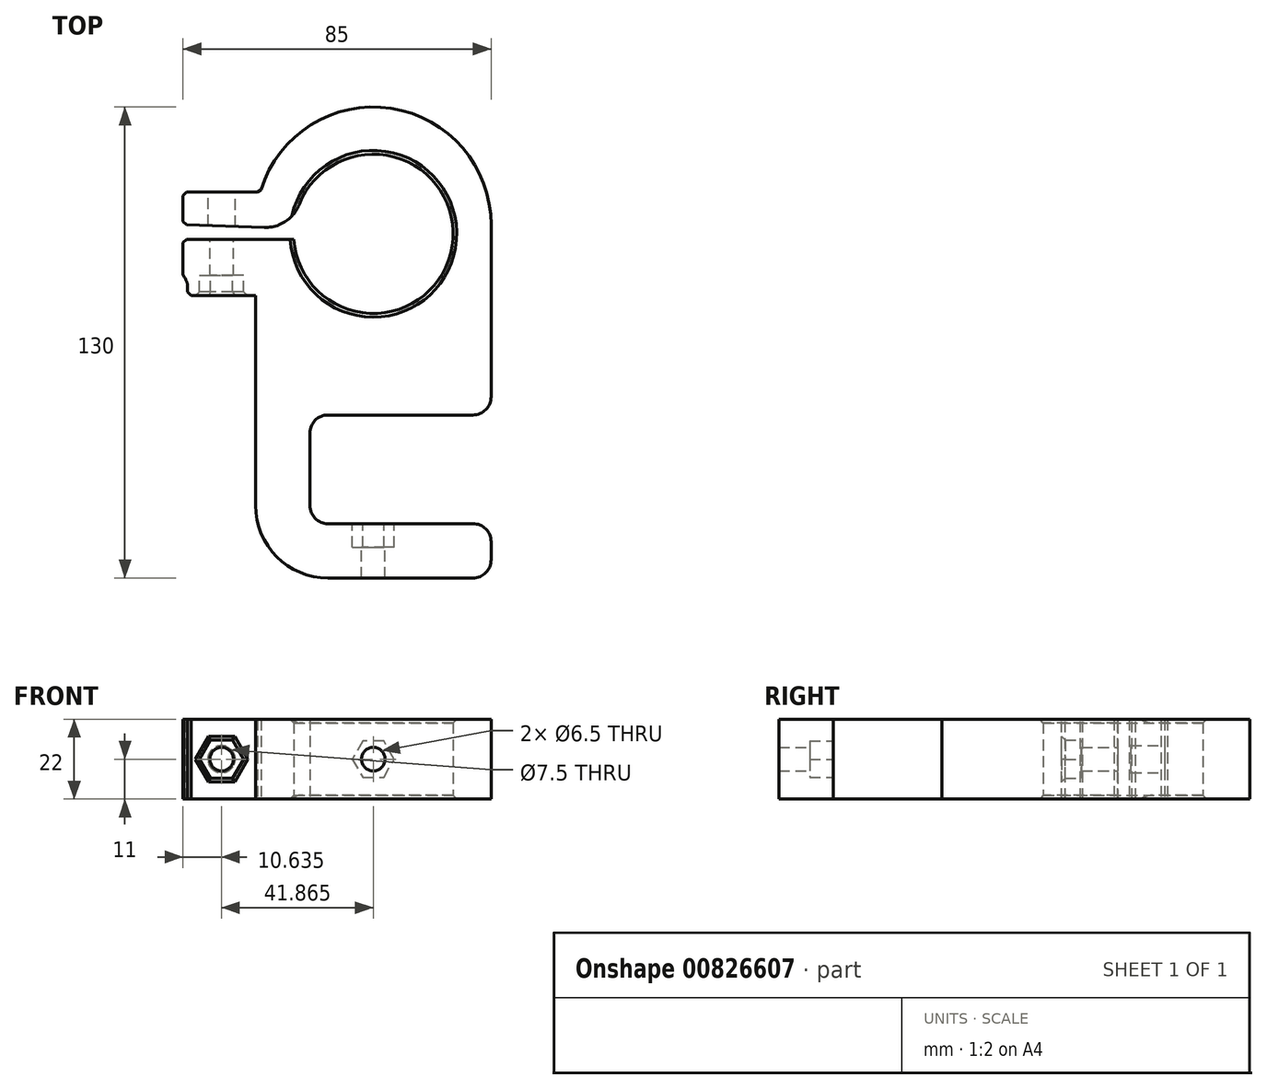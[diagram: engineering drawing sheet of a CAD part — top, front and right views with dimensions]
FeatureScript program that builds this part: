
annotation { "Feature Type Name" : "Feature", "Feature Type Description" : "" }
export const myFeature = defineFeature(function(context is Context, id is Id, definition is map)
    precondition{}
    {
        {
            var Q0;
            Q0=qCreatedBy(makeId("Top.planeOp"),FACE);
            var sketch = newSketch(context, id + "F0", { "sketchPlane" : qUnion([Q0])});
            skLineSegment(sketch, "E0", {"start": v(0, 0) * mm, "end": v(-50, 0) * mm});
            skLineSegment(sketch, "E1", {"start": v(-50, 0) * mm, "end": v(-50, 30) * mm});
            skLineSegment(sketch, "E2", {"start": v(-50, 30) * mm, "end": v(0, 30) * mm});
            skLineSegment(sketch, "E3", {"start": v(0, 0) * mm, "end": v(0, -15) * mm});
            skLineSegment(sketch, "E4", {"start": v(0, -15) * mm, "end": v(-65, -15) * mm});
            skLineSegment(sketch, "E5", {"start": v(-65, -15) * mm, "end": v(-65, 78.5) * mm});
            skLineSegment(sketch, "E6", {"start": v(-65, 78.5) * mm, "end": v(-54.45, 78.5) * mm});
            skArc(sketch, "E7", {"start": v(-54.45, 78.5) * mm, "mid": v(-10.5, 80) * mm, "end": v(-54.45, 81.5) * mm});
            skLineSegment(sketch, "E8", {"start": v(-54.45, 81.5) * mm, "end": v(-65, 81.5) * mm});
            skLineSegment(sketch, "E9", {"start": v(-65, 81.5) * mm, "end": v(-65, 115) * mm});
            skLineSegment(sketch, "E10", {"start": v(-65, 115) * mm, "end": v(0, 115) * mm});
            skLineSegment(sketch, "E11", {"start": v(0, 115) * mm, "end": v(0, 30) * mm});
            skSolve(sketch);
        }
        {
            var Q0;
            Q0 = qSketchRegion(id + "F0", true);
            extrude(context, id + "F1", {"entities" : qUnion([Q0]), "depth" : 22 * mm, "offsetDistance" : 25 * mm});
        }
        {
            var Q0;
            Q0=makeQuery(id+"F1.opExtrude","SWEPT_EDGE",EDGE,{"disambiguationData":[OSD([sQuery(id+"F0.wireOp",EDGE,"E9"),sQuery(id+"F0.wireOp",EDGE,"E10")])]});
            var Q1;
            Q1=makeQuery(id+"F1.opExtrude","SWEPT_EDGE",EDGE,{"disambiguationData":[OSD([sQuery(id+"F0.wireOp",EDGE,"E10"),sQuery(id+"F0.wireOp",EDGE,"E11")])]});
            fillet(context, id + "F2", {"entities" : qUnion([Q0, Q1]), "radius" : 32.5 * mm, "tangentPropagation" : true, "allowEdgeOverflow" : false});
        }
        {
            var Q0;
            Q0=makeQuery(id+"F1.opExtrude","CAP_EDGE",EDGE,{"disambiguationData":[OSD([sQuery(id+"F0.wireOp",EDGE,"E7")])],"isStart":false});
            var Q1;
            Q1=makeQuery(id+"F1.opExtrude","CAP_EDGE",EDGE,{"disambiguationData":[OSD([sQuery(id+"F0.wireOp",EDGE,"E7")])],"isStart":true});
            chamfer(context, id + "F3", {"entities" : qUnion([Q0, Q1]), "width" : 1 * mm, "tangentPropagation" : true});
        }
        {
            var Q0;
            Q0=makeQuery(id+"F1.opExtrude","SWEPT_FACE",FACE,{"disambiguationData":[OSD([sQuery(id+"F0.wireOp",EDGE,"E5")])]});
            var sketch = newSketch(context, id + "F4", { "sketchPlane" : qUnion([Q0])});
            skLineSegment(sketch, "E12.bottom", {"start": v(-78.5, 0) * mm, "end": v(-68.5, 0) * mm});
            skLineSegment(sketch, "E12.top", {"start": v(-78.5, 22) * mm, "end": v(-68.5, 22) * mm});
            skLineSegment(sketch, "E12.left", {"start": v(-78.5, 0) * mm, "end": v(-78.5, 22) * mm});
            skLineSegment(sketch, "E12.right", {"start": v(-68.5, 0) * mm, "end": v(-68.5, 22) * mm});
            skSolve(sketch);
        }
        {
            var Q0;
            Q0 = qSketchRegion(id + "F4", true);
            extrude(context, id + "F5", {"entities" : qUnion([Q0]), "operationType" : NewBodyOperationType.ADD, "depth" : 20 * mm, "offsetDistance" : 25 * mm});
        }
        {
            var Q0;
            Q0=makeQuery(id+"F1.opExtrude","SWEPT_FACE",FACE,{"disambiguationData":[OSD([sQuery(id+"F0.wireOp",EDGE,"E9")])]});
            var sketch = newSketch(context, id + "F6", { "sketchPlane" : qUnion([Q0])});
            skLineSegment(sketch, "E13.bottom", {"start": v(-81.5, 0) * mm, "end": v(-91.5, 0) * mm});
            skLineSegment(sketch, "E13.top", {"start": v(-81.5, 22) * mm, "end": v(-91.5, 22) * mm});
            skLineSegment(sketch, "E13.left", {"start": v(-81.5, 0) * mm, "end": v(-81.5, 22) * mm});
            skLineSegment(sketch, "E13.right", {"start": v(-91.5, 0) * mm, "end": v(-91.5, 22) * mm});
            skSolve(sketch);
        }
        {
            var Q0;
            Q0 = qSketchRegion(id + "F6", true);
            extrude(context, id + "F7", {"entities" : qUnion([Q0]), "operationType" : NewBodyOperationType.ADD, "depth" : 20 * mm, "offsetDistance" : 25 * mm, "hasSecondDirection" : true, "secondDirectionOppositeDirection" : true, "secondDirectionDepth" : 2 * mm});
        }
        {
            var Q0;
            Q0=makeQuery(id+"F7.opExtrude","CAP_EDGE",EDGE,{"disambiguationData":[OSD([sQuery(id+"F6.wireOp",EDGE,"E13.left")])],"isStart":false});
            chamfer(context, id + "F8", {"entities" : qUnion([Q0]), "chamferType" : ChamferType.TWO_OFFSETS, "width1" : 30 * mm, "oppositeDirection" : false, "width2" : 1 * mm, "tangentPropagation" : true});
        }
        {
            var Q0;
            Q0=makeQuery(id+"F7.opExtrude","SWEPT_FACE",FACE,{"disambiguationData":[OSD([sQuery(id+"F6.wireOp",EDGE,"E13.right")])]});
            var sketch = newSketch(context, id + "F9", { "sketchPlane" : qUnion([Q0])});
            skLineSegment(sketch, "E14", {"start": v(85, 0) * mm, "end": v(63.73, 22) * mm, "construction": true});
            skCircle(sketch, "E15", {"center": v(74.36, 11) * mm, "radius": 3.25 * mm});
            skSolve(sketch);
        }
        {
            var Q0;
            Q0 = qSketchRegion(id + "F9", true);
            extrude(context, id + "F10", {"entities" : qUnion([Q0]), "operationType" : NewBodyOperationType.REMOVE, "endBound" : BoundingType.THROUGH_ALL, "oppositeDirection" : true, "depth" : 25 * mm, "offsetDistance" : 25 * mm});
        }
        {
            var Q0;
            Q0=makeQuery(id+"F5.opExtrude","SWEPT_FACE",FACE,{"disambiguationData":[OSD([sQuery(id+"F4.wireOp",EDGE,"E12.right")])]});
            var sketch = newSketch(context, id + "F11", { "sketchPlane" : qUnion([Q0])});
            skCircle(sketch, "E16.cCircle", {"center": v(-74.36, 11) * mm, "radius": 5.25 * mm, "construction": true});
            skLineSegment(sketch, "E16.0", {"start": v(-77.4, 16.25) * mm, "end": v(-71.33, 16.25) * mm});
            skLineSegment(sketch, "E16.1", {"start": v(-71.33, 16.25) * mm, "end": v(-68.3, 11) * mm});
            skLineSegment(sketch, "E16.2", {"start": v(-68.3, 11) * mm, "end": v(-71.33, 5.75) * mm});
            skLineSegment(sketch, "E16.3", {"start": v(-71.33, 5.75) * mm, "end": v(-77.4, 5.75) * mm});
            skLineSegment(sketch, "E16.4", {"start": v(-77.4, 5.75) * mm, "end": v(-80.43, 11) * mm});
            skLineSegment(sketch, "E16.5", {"start": v(-80.43, 11) * mm, "end": v(-77.4, 16.25) * mm});
            skPoint(sketch, "E16.0.midPoint", {"position": v(-74.36, 16.25) * mm});
            skLineSegment(sketch, "E17.bottom", {"start": v(-83.73, 22) * mm, "end": v(-65, 22) * mm});
            skLineSegment(sketch, "E17.top", {"start": v(-83.73, 0) * mm, "end": v(-65, 0) * mm});
            skLineSegment(sketch, "E17.left", {"start": v(-83.73, 22) * mm, "end": v(-83.73, 0) * mm});
            skLineSegment(sketch, "E17.right", {"start": v(-65, 22) * mm, "end": v(-65, 0) * mm});
            skSolve(sketch);
        }
        {
            var Q0;
            Q0 = qSketchRegion(id + "F11", true);
            extrude(context, id + "F12", {"entities" : qUnion([Q0]), "operationType" : NewBodyOperationType.ADD, "depth" : 5.5 * mm, "offsetDistance" : 25 * mm});
        }
        {
            var Q0;
            Q0=makeQuery(id+"F1.opExtrude","SWEPT_EDGE",EDGE,{"disambiguationData":[OSD([sQuery(id+"F0.wireOp",EDGE,"E4"),sQuery(id+"F0.wireOp",EDGE,"E5")])]});
            fillet(context, id + "F13", {"entities" : qUnion([Q0]), "radius" : 20 * mm, "tangentPropagation" : true, "allowEdgeOverflow" : false});
        }
        {
            var Q0;
            Q0=makeQuery(id+"F1.opExtrude","SWEPT_EDGE",EDGE,{"disambiguationData":[OSD([sQuery(id+"F0.wireOp",EDGE,"E0"),sQuery(id+"F0.wireOp",EDGE,"E1")])]});
            var Q1;
            Q1=makeQuery(id+"F1.opExtrude","SWEPT_EDGE",EDGE,{"disambiguationData":[OSD([sQuery(id+"F0.wireOp",EDGE,"E1"),sQuery(id+"F0.wireOp",EDGE,"E2")])]});
            fillet(context, id + "F14", {"entities" : qUnion([Q0, Q1]), "radius" : 5 * mm, "tangentPropagation" : true, "allowEdgeOverflow" : false});
        }
        {
            var Q0;
            Q0=makeQuery(id+"F1.opExtrude","SWEPT_FACE",FACE,{"disambiguationData":[OSD([sQuery(id+"F0.wireOp",EDGE,"E0")])]});
            var sketch = newSketch(context, id + "F15", { "sketchPlane" : qUnion([Q0])});
            skLineSegment(sketch, "E18", {"start": v(0, 11) * mm, "end": v(45, 11) * mm, "construction": true});
            skLineSegment(sketch, "E19.0.0", {"start": v(54.45, 21) * mm, "end": v(54.45, 1) * mm});
            skLineSegment(sketch, "E19.0.1", {"start": v(54.45, 1) * mm, "end": v(10.5, 1) * mm, "construction": true});
            skLineSegment(sketch, "E19.0.2", {"start": v(54.45, 1) * mm, "end": v(54.45, 21) * mm, "construction": true});
            skLineSegment(sketch, "E19.0.3", {"start": v(54.45, 21) * mm, "end": v(10.5, 21) * mm, "construction": true});
            skCircle(sketch, "E20", {"center": v(32.5, 11) * mm, "radius": 3.25 * mm});
            skSolve(sketch);
        }
        {
            var Q0;
            Q0 = qSketchRegion(id + "F15", true);
            var Q1;
            Q1=makeQuery(id+"F1.opExtrude","SWEPT_FACE",FACE,{"disambiguationData":[OSD([sQuery(id+"F0.wireOp",EDGE,"E4")])]});
            extrude(context, id + "F16", {"entities" : qUnion([Q0]), "operationType" : NewBodyOperationType.REMOVE, "endBound" : BoundingType.UP_TO_SURFACE, "oppositeDirection" : true, "depth" : 25 * mm, "endBoundEntityFace" : qUnion([Q1]), "offsetDistance" : 25 * mm});
        }
        {
            var Q0;
            Q0=makeQuery(id+"F1.opExtrude","SWEPT_FACE",FACE,{"disambiguationData":[OSD([sQuery(id+"F0.wireOp",EDGE,"E0")])]});
            var sketch = newSketch(context, id + "F17", { "sketchPlane" : qUnion([Q0])});
            skCircle(sketch, "E21.cCircle", {"center": v(32.5, 11) * mm, "radius": 5 * mm, "construction": true});
            skLineSegment(sketch, "E21.0", {"start": v(35.39, 6) * mm, "end": v(29.61, 6) * mm});
            skLineSegment(sketch, "E21.1", {"start": v(29.61, 6) * mm, "end": v(26.73, 11) * mm});
            skLineSegment(sketch, "E21.2", {"start": v(26.73, 11) * mm, "end": v(29.61, 16) * mm});
            skLineSegment(sketch, "E21.3", {"start": v(29.61, 16) * mm, "end": v(35.39, 16) * mm});
            skLineSegment(sketch, "E21.4", {"start": v(35.39, 16) * mm, "end": v(38.27, 11) * mm});
            skLineSegment(sketch, "E21.5", {"start": v(38.27, 11) * mm, "end": v(35.39, 6) * mm});
            skPoint(sketch, "E21.0.midPoint", {"position": v(32.5, 6) * mm});
            skSolve(sketch);
        }
        {
            var Q0;
            Q0 = qSketchRegion(id + "F17", true);
            extrude(context, id + "F18", {"entities" : qUnion([Q0]), "operationType" : NewBodyOperationType.REMOVE, "oppositeDirection" : true, "depth" : 6.5 * mm, "offsetDistance" : 25 * mm});
        }
        {
            var Q0;
            Q0=makeQuery(id+"F18.boolean.opBoolean","COPY",EDGE,{"derivedFrom":makeQuery(id+"F18.opExtrude","CAP_EDGE",EDGE,{"disambiguationData":[OSD([sQuery(id+"F17.wireOp",EDGE,"E21.0")])],"isStart":true})});
            var Q1;
            Q1=makeQuery(id+"F18.boolean.opBoolean","COPY",EDGE,{"derivedFrom":makeQuery(id+"F18.opExtrude","CAP_EDGE",EDGE,{"disambiguationData":[OSD([sQuery(id+"F17.wireOp",EDGE,"E21.1")])],"isStart":true})});
            var Q2;
            Q2=makeQuery(id+"F18.boolean.opBoolean","COPY",EDGE,{"derivedFrom":makeQuery(id+"F18.opExtrude","CAP_EDGE",EDGE,{"disambiguationData":[OSD([sQuery(id+"F17.wireOp",EDGE,"E21.2")])],"isStart":true})});
            var Q3;
            Q3=makeQuery(id+"F18.boolean.opBoolean","COPY",EDGE,{"derivedFrom":makeQuery(id+"F18.opExtrude","CAP_EDGE",EDGE,{"disambiguationData":[OSD([sQuery(id+"F17.wireOp",EDGE,"E21.3")])],"isStart":true})});
            var Q4;
            Q4=makeQuery(id+"F18.boolean.opBoolean","COPY",EDGE,{"derivedFrom":makeQuery(id+"F18.opExtrude","CAP_EDGE",EDGE,{"disambiguationData":[OSD([sQuery(id+"F17.wireOp",EDGE,"E21.4")])],"isStart":true})});
            var Q5;
            Q5=makeQuery(id+"F18.boolean.opBoolean","COPY",EDGE,{"derivedFrom":makeQuery(id+"F18.opExtrude","CAP_EDGE",EDGE,{"disambiguationData":[OSD([sQuery(id+"F17.wireOp",EDGE,"E21.5")])],"isStart":true})});
            var Q6;
            Q6=makeQuery(id+"F12.opExtrude","CAP_EDGE",EDGE,{"disambiguationData":[OSD([sQuery(id+"F11.wireOp",EDGE,"E16.3")])],"isStart":false});
            var Q7;
            Q7=makeQuery(id+"F12.opExtrude","CAP_EDGE",EDGE,{"disambiguationData":[OSD([sQuery(id+"F11.wireOp",EDGE,"E16.2")])],"isStart":false});
            var Q8;
            Q8=makeQuery(id+"F12.opExtrude","CAP_EDGE",EDGE,{"disambiguationData":[OSD([sQuery(id+"F11.wireOp",EDGE,"E16.1")])],"isStart":false});
            var Q9;
            Q9=makeQuery(id+"F12.opExtrude","CAP_EDGE",EDGE,{"disambiguationData":[OSD([sQuery(id+"F11.wireOp",EDGE,"E16.0")])],"isStart":false});
            var Q10;
            Q10=makeQuery(id+"F12.opExtrude","CAP_EDGE",EDGE,{"disambiguationData":[OSD([sQuery(id+"F11.wireOp",EDGE,"E16.5")])],"isStart":false});
            var Q11;
            Q11=makeQuery(id+"F12.opExtrude","CAP_EDGE",EDGE,{"disambiguationData":[OSD([sQuery(id+"F11.wireOp",EDGE,"E16.4")])],"isStart":false});
            chamfer(context, id + "F19", {"entities" : qUnion([Q0, Q1, Q2, Q3, Q4, Q5, Q6, Q7, Q8, Q9, Q10, Q11]), "width" : 1 * mm, "tangentPropagation" : true});
        }
        {
            var Q0;
            Q0=makeQuery(id+"F12.opExtrude","CAP_EDGE",EDGE,{"disambiguationData":[OSD([sQuery(id+"F11.wireOp",EDGE,"E17.left")])],"isStart":true});
            fillet(context, id + "F20", {"entities" : qUnion([Q0]), "radius" : 5 * mm, "tangentPropagation" : true, "allowEdgeOverflow" : false});
        }
        {
            var Q0;
            Q0=makeQuery(id+"F7.opExtrude","CAP_EDGE",EDGE,{"disambiguationData":[OSD([sQuery(id+"F6.wireOp",EDGE,"E13.right")])],"isStart":false});
            var Q1;
            {var subQ0=sQuery(id+"F6.wireOp",EDGE,"E13.left");Q1=makeQuery(id+"F8.opChamfer","BLEND_EDGE",EDGE,{"blendedFrom":[makeQuery(id+"F7.opExtrude","CAP_EDGE",EDGE,{"disambiguationData":[OSD([subQ0])],"isStart":false}),makeQuery(id+"F7.opExtrude","CAP_FACE",FACE,{"disambiguationData":[OSD([sQuery(id+"F6.wireOp",EDGE,"E13.bottom"),sQuery(id+"F6.wireOp",EDGE,"E13.top"),subQ0,sQuery(id+"F6.wireOp",EDGE,"E13.right")])],"isStart":false})],"blendedInto":[makeQuery(id+"F7.opExtrude","CAP_FACE",FACE,{"disambiguationData":[OSD([sQuery(id+"F6.wireOp",EDGE,"E13.bottom"),sQuery(id+"F6.wireOp",EDGE,"E13.top"),subQ0,sQuery(id+"F6.wireOp",EDGE,"E13.right")])],"isStart":false})]});}
            var Q2;
            Q2=makeQuery(id+"F5.opExtrude","CAP_EDGE",EDGE,{"disambiguationData":[OSD([sQuery(id+"F4.wireOp",EDGE,"E12.left")])],"isStart":false});
            var Q3;
            Q3=makeQuery(id+"F20.opFillet","BLEND_EDGE",EDGE,{"blendedFrom":[makeQuery(id+"F12.opExtrude","CAP_EDGE",EDGE,{"disambiguationData":[OSD([sQuery(id+"F11.wireOp",EDGE,"E17.left")])],"isStart":true}),makeQuery(id+"F5.opExtrude","CAP_FACE",FACE,{"disambiguationData":[OSD([sQuery(id+"F4.wireOp",EDGE,"E12.bottom"),sQuery(id+"F4.wireOp",EDGE,"E12.top"),sQuery(id+"F4.wireOp",EDGE,"E12.left"),sQuery(id+"F4.wireOp",EDGE,"E12.right")])],"isStart":false})],"blendedInto":[makeQuery(id+"F5.opExtrude","CAP_FACE",FACE,{"disambiguationData":[OSD([sQuery(id+"F4.wireOp",EDGE,"E12.bottom"),sQuery(id+"F4.wireOp",EDGE,"E12.top"),sQuery(id+"F4.wireOp",EDGE,"E12.left"),sQuery(id+"F4.wireOp",EDGE,"E12.right")])],"isStart":false})]});
            var Q4;
            Q4=makeQuery(id+"F12.opExtrude","CAP_EDGE",EDGE,{"disambiguationData":[OSD([sQuery(id+"F11.wireOp",EDGE,"E17.left")])],"isStart":false});
            chamfer(context, id + "F21", {"entities" : qUnion([Q0, Q1, Q2, Q3, Q4]), "width" : 1 * mm, "tangentPropagation" : true});
        }
        {
            var Q0;
            Q0=makeQuery(id+"F7.boolean.opBoolean","INTERSECT",EDGE,{"derivedFrom":[makeQuery(id+"F2.opFillet","BLEND_FACE",FACE,{"disambiguationData":[OSD([sQuery(id+"F0.wireOp",EDGE,"E10"),sQuery(id+"F0.wireOp",EDGE,"E11")])]}),makeQuery(id+"F7.opExtrude","SWEPT_FACE",FACE,{"disambiguationData":[OSD([sQuery(id+"F6.wireOp",EDGE,"E13.right")])]})]});
            var Q1;
            Q1=makeQuery(id+"F12.opExtrude","CAP_EDGE",EDGE,{"disambiguationData":[OSD([sQuery(id+"F11.wireOp",EDGE,"E17.right")])],"isStart":false});
            chamfer(context, id + "F22", {"entities" : qUnion([Q0, Q1]), "width" : 1 * mm, "tangentPropagation" : true});
        }
        {
            var Q0;
            Q0=makeQuery(id+"F1.opExtrude","SWEPT_EDGE",EDGE,{"disambiguationData":[OSD([sQuery(id+"F0.wireOp",EDGE,"E2"),sQuery(id+"F0.wireOp",EDGE,"E11")])]});
            var Q1;
            Q1=makeQuery(id+"F1.opExtrude","SWEPT_EDGE",EDGE,{"disambiguationData":[OSD([sQuery(id+"F0.wireOp",EDGE,"E0"),sQuery(id+"F0.wireOp",EDGE,"E3")])]});
            fillet(context, id + "F23", {"entities" : qUnion([Q0, Q1]), "radius" : 5 * mm, "tangentPropagation" : true, "allowEdgeOverflow" : false});
        }
        {
            var Q0;
            Q0=makeQuery(id+"F1.opExtrude","SWEPT_EDGE",EDGE,{"disambiguationData":[OSD([sQuery(id+"F0.wireOp",EDGE,"E7"),sQuery(id+"F0.wireOp",EDGE,"E8")])]});
            fillet(context, id + "F24", {"entities" : qUnion([Q0]), "radius" : 10 * mm, "tangentPropagation" : true, "allowEdgeOverflow" : false});
        }
        {
            var Q0;
            Q0=makeQuery(id+"F7.opExtrude","SWEPT_FACE",FACE,{"disambiguationData":[OSD([sQuery(id+"F6.wireOp",EDGE,"E13.right")])]});
            var sketch = newSketch(context, id + "F25", { "sketchPlane" : qUnion([Q0])});
            skCircle(sketch, "E22", {"center": v(74.36, 11) * mm, "radius": 3.75 * mm});
            skSolve(sketch);
        }
        {
            var Q0;
            Q0 = qSketchRegion(id + "F25", true);
            var Q1;
            Q1=makeQuery(id+"F8.opChamfer","BLEND_FACE",FACE,{"disambiguationData":[OSD([sQuery(id+"F6.wireOp",EDGE,"E13.left")])]});
            extrude(context, id + "F26", {"entities" : qUnion([Q0]), "operationType" : NewBodyOperationType.REMOVE, "endBound" : BoundingType.UP_TO_SURFACE, "oppositeDirection" : true, "depth" : 25 * mm, "endBoundEntityFace" : qUnion([Q1]), "offsetDistance" : 25 * mm});
        }
        {
            var Q0;
            Q0=makeQuery(id+"F1.opExtrude","SWEPT_EDGE",EDGE,{"disambiguationData":[OSD([sQuery(id+"F0.wireOp",EDGE,"E3"),sQuery(id+"F0.wireOp",EDGE,"E4")])]});
            fillet(context, id + "F27", {"entities" : qUnion([Q0]), "radius" : 5 * mm, "tangentPropagation" : true, "allowEdgeOverflow" : false});
        }
    });
